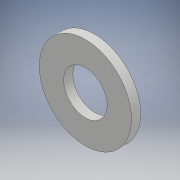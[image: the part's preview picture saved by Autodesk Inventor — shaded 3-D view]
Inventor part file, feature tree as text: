
AUTODESK INVENTOR PART (.ipt)
format: ipt  version: 2018 (Build 220112000, 112)  size: 97,792 bytes
history: native  units: mm
features: extrude x1, sketch x1
ambient origin geometry x8: Origin, YZ Plane, XZ Plane, XY Plane, X Axis, Y Axis, Z Axis, Center Point
bodies: Solid1 (feature_tree)
feature tree (2):
  extrude  "Extrusion1"  Depth=1.8mm
  sketch  "Sketch1"  dims[d0=18.0mm d1=8.5mm d2=1.8mm d3=0.0mm]
